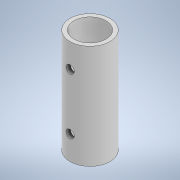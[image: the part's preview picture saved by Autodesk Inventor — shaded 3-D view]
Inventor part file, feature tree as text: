
AUTODESK INVENTOR PART (.ipt)
format: ipt  version: 2022 (Build 260153000, 153)  size: 184,320 bytes
history: native  units: mm
features: extrude x2, sketch x2
ambient origin geometry x8: Origin, YZ Plane, XZ Plane, XY Plane, X Axis, Y Axis, Z Axis, Center Point
bodies: Body1 (feature_tree)
feature tree (4):
  extrude  "Extrusion10"  Depth=8.0mm
  extrude  "Extrusion11"  Depth=6.0mm
  sketch  "Sketch9"  dims[d31=34.456mm d140=8.0mm]
  sketch  "Sketch10"  dims[d141=26.0mm d142=0.0mm d143=6.0mm d144=2.0mm d145=6.0mm d146=2.0mm d147=24.0mm d148=0.0mm d149=10.0mm]
